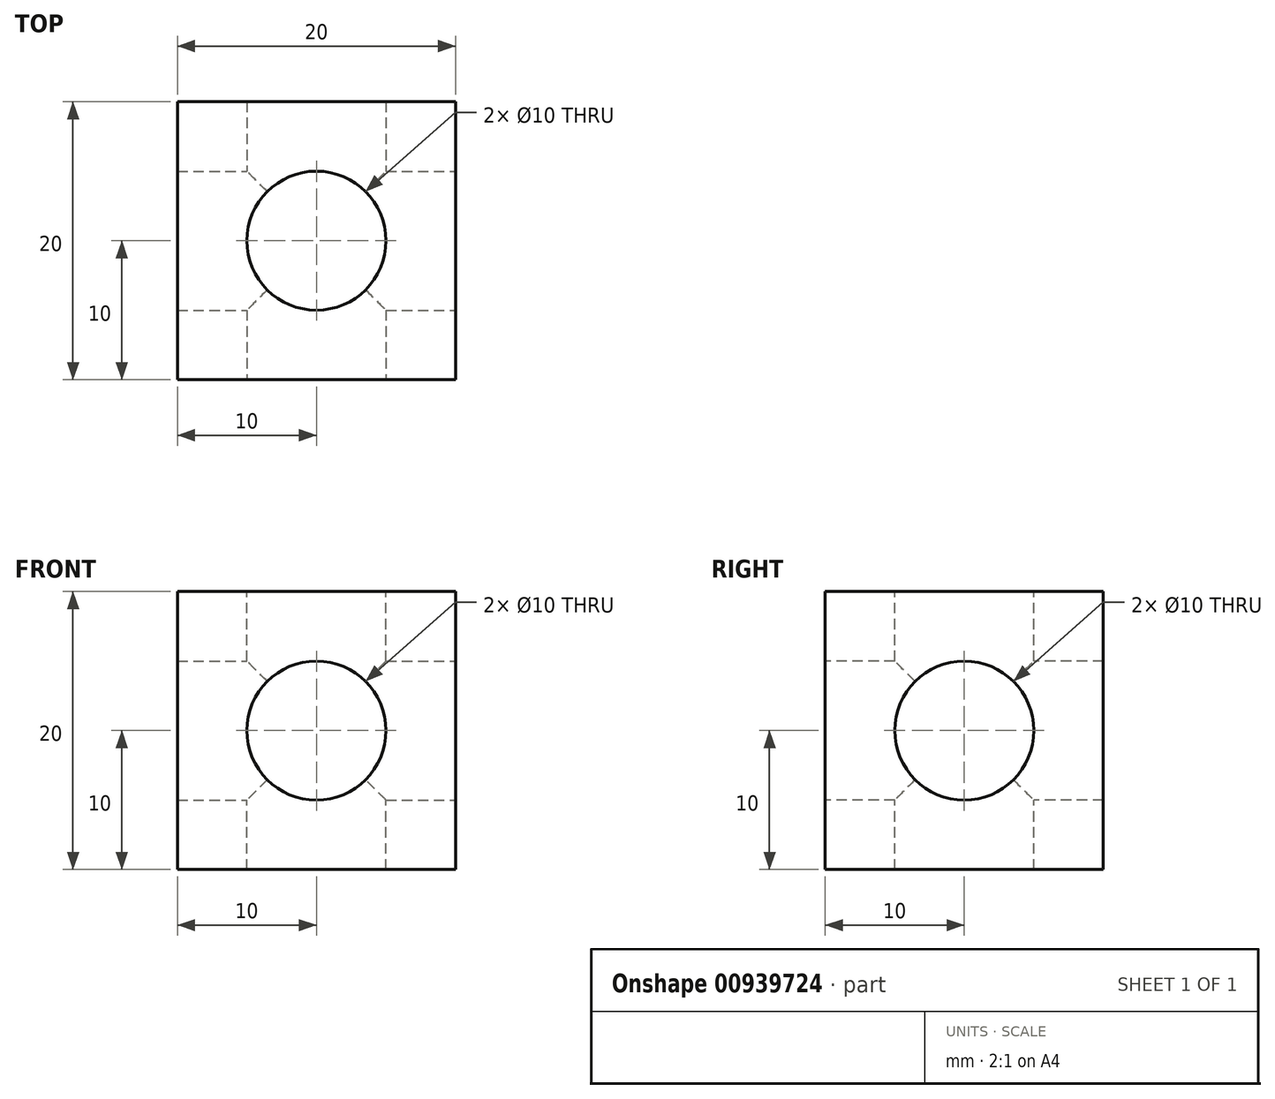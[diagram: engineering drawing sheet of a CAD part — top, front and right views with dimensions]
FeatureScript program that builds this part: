
annotation { "Feature Type Name" : "Feature", "Feature Type Description" : "" }
export const myFeature = defineFeature(function(context is Context, id is Id, definition is map)
    precondition{}
    {
        {
            var Q0;
            Q0=qCreatedBy(makeId("Top.planeOp"),FACE);
            var sketch = newSketch(context, id + "F0", { "sketchPlane" : qUnion([Q0])});
            skLineSegment(sketch, "E0.bottom", {"start": v(0, 0) * mm, "end": v(20, 0) * mm});
            skLineSegment(sketch, "E0.top", {"start": v(0, 20) * mm, "end": v(20, 20) * mm});
            skLineSegment(sketch, "E0.left", {"start": v(0, 0) * mm, "end": v(0, 20) * mm});
            skLineSegment(sketch, "E0.right", {"start": v(20, 0) * mm, "end": v(20, 20) * mm});
            skSolve(sketch);
        }
        {
            var Q0;
            Q0=makeQuery(id+"F0.imprint","IMPRINT",FACE,{"disambiguationData":[TD([[makeQuery(id+"F0.imprint","IMPRINT",EDGE,{"derivedFrom":sQuery(id+"F0.wireOp",EDGE,"E0.bottom")}),1.0]])]});
            extrude(context, id + "F1", {"entities" : qUnion([Q0]), "depth" : 20 * mm, "offsetDistance" : 25 * mm});
        }
        {
            var Q0;
            Q0=makeQuery(id+"F1.opExtrude","CAP_FACE",FACE,{"disambiguationData":[OSD([sQuery(id+"F0.wireOp",EDGE,"E0.bottom"),sQuery(id+"F0.wireOp",EDGE,"E0.top"),sQuery(id+"F0.wireOp",EDGE,"E0.left"),sQuery(id+"F0.wireOp",EDGE,"E0.right")])],"isStart":false});
            var sketch = newSketch(context, id + "F2", { "sketchPlane" : qUnion([Q0])});
            skLineSegment(sketch, "E1", {"start": v(0, 20) * mm, "end": v(20, 0) * mm, "construction": true});
            skCircle(sketch, "E2", {"center": v(10, 10) * mm, "radius": 5 * mm});
            skSolve(sketch);
        }
        {
            var Q0;
            Q0=makeQuery(id+"F2.imprint","IMPRINT",FACE,{"disambiguationData":[TD([[makeQuery(id+"F2.imprint","IMPRINT",EDGE,{"derivedFrom":sQuery(id+"F2.wireOp",EDGE,"E2")}),1.0]])]});
            var Q1;
            Q1=sQuery(id+"F2.wireOp",EDGE,"E2");
            extrude(context, id + "F3", {"entities" : qUnion([Q0]), "operationType" : NewBodyOperationType.REMOVE, "surfaceEntities" : qUnion([Q1]), "endBound" : BoundingType.SYMMETRIC, "oppositeDirection" : true, "depth" : 50 * mm, "offsetDistance" : 25 * mm});
        }
        {
            var Q0;
            Q0=makeQuery(id+"F1.opExtrude","SWEPT_FACE",FACE,{"disambiguationData":[OSD([sQuery(id+"F0.wireOp",EDGE,"E0.bottom")])]});
            var sketch = newSketch(context, id + "F4", { "sketchPlane" : qUnion([Q0])});
            skLineSegment(sketch, "E3", {"start": v(20, 20) * mm, "end": v(0, 0) * mm, "construction": true});
            skCircle(sketch, "E4", {"center": v(10, 10) * mm, "radius": 5 * mm});
            skSolve(sketch);
        }
        {
            var Q0;
            Q0=makeQuery(id+"F4.imprint","IMPRINT",FACE,{"disambiguationData":[TD([[makeQuery(id+"F4.imprint","IMPRINT",EDGE,{"derivedFrom":sQuery(id+"F4.wireOp",EDGE,"E4")}),1.0]])]});
            extrude(context, id + "F5", {"entities" : qUnion([Q0]), "operationType" : NewBodyOperationType.REMOVE, "oppositeDirection" : true, "depth" : 25 * mm, "offsetDistance" : 25 * mm});
        }
        {
            var Q0;
            Q0=makeQuery(id+"F1.opExtrude","SWEPT_FACE",FACE,{"disambiguationData":[OSD([sQuery(id+"F0.wireOp",EDGE,"E0.right")])]});
            var sketch = newSketch(context, id + "F6", { "sketchPlane" : qUnion([Q0])});
            skLineSegment(sketch, "E5", {"start": v(20, 20) * mm, "end": v(0, 0) * mm, "construction": true});
            skCircle(sketch, "E6", {"center": v(10, 10) * mm, "radius": 5 * mm});
            skSolve(sketch);
        }
        {
            var Q0;
            Q0=makeQuery(id+"F6.imprint","IMPRINT",FACE,{"disambiguationData":[TD([[makeQuery(id+"F6.imprint","IMPRINT",EDGE,{"derivedFrom":sQuery(id+"F6.wireOp",EDGE,"E6")}),1.0]])]});
            extrude(context, id + "F7", {"entities" : qUnion([Q0]), "operationType" : NewBodyOperationType.REMOVE, "oppositeDirection" : true, "depth" : 25 * mm, "offsetDistance" : 25 * mm});
        }
    });
